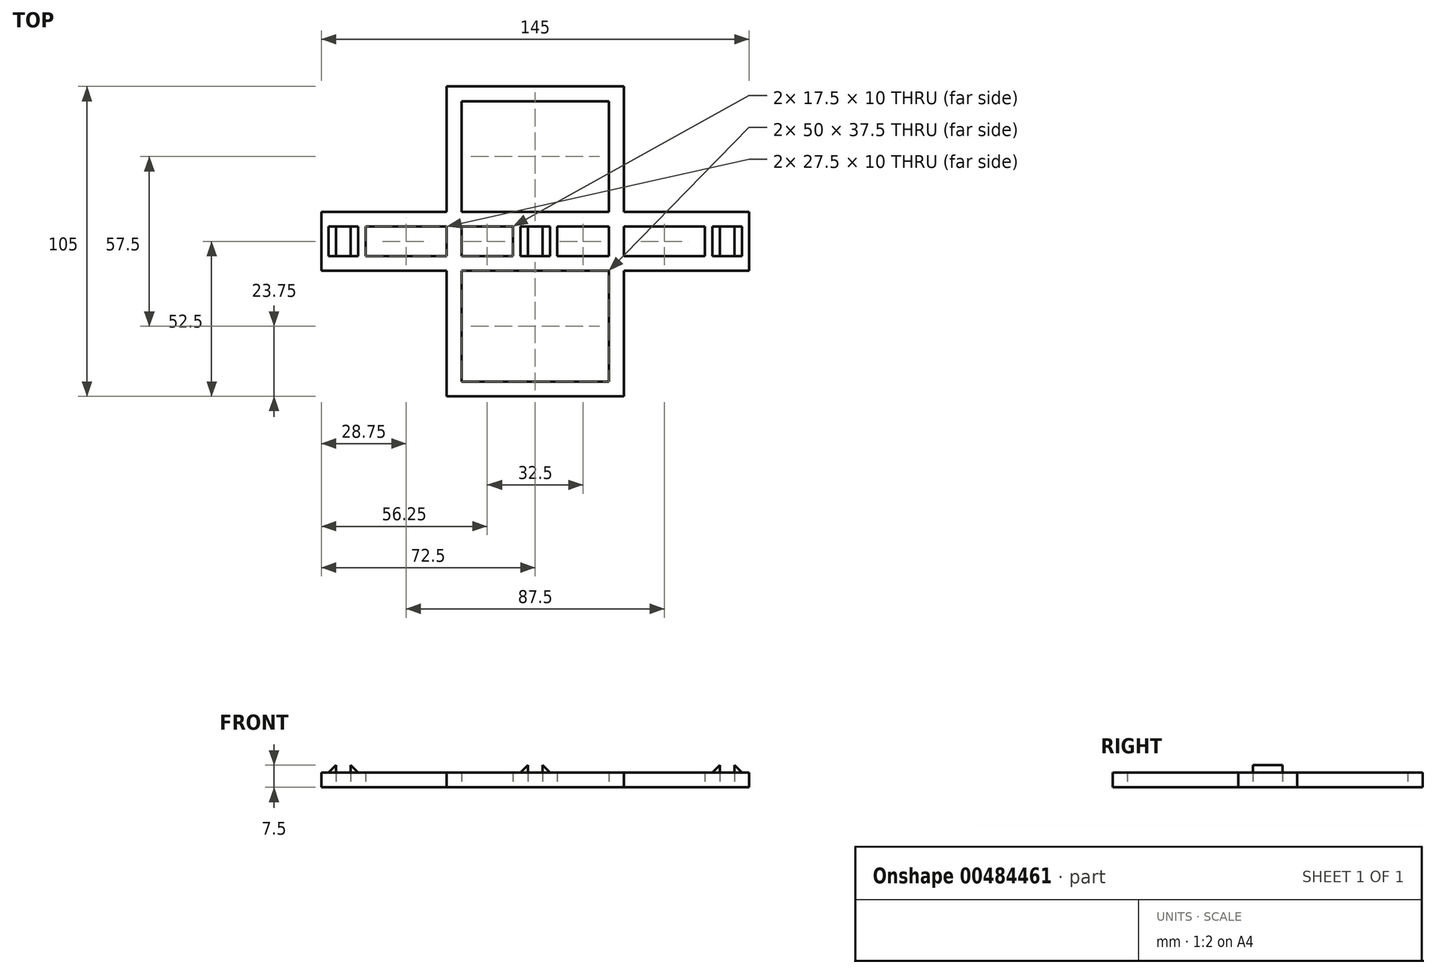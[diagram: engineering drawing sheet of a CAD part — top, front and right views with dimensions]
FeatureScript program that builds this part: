
annotation { "Feature Type Name" : "Feature", "Feature Type Description" : "" }
export const myFeature = defineFeature(function(context is Context, id is Id, definition is map)
    precondition{}
    {
        {
            var Q0;
            Q0=qCreatedBy(makeId("Top.planeOp"),FACE);
            var sketch = newSketch(context, id + "F0", { "sketchPlane" : qUnion([Q0])});
            skLineSegment(sketch, "E0.bottom", {"start": v(-2.5, 5) * mm, "end": v(2.5, 5) * mm});
            skLineSegment(sketch, "E0.top", {"start": v(-2.5, -5) * mm, "end": v(2.5, -5) * mm});
            skLineSegment(sketch, "E0.left", {"start": v(-2.5, 5) * mm, "end": v(-2.5, -5) * mm});
            skLineSegment(sketch, "E0.right", {"start": v(2.5, 5) * mm, "end": v(2.5, -5) * mm});
            skLineSegment(sketch, "E1.bottom", {"start": v(62.5, 5) * mm, "end": v(67.5, 5) * mm});
            skLineSegment(sketch, "E1.top", {"start": v(62.5, -5) * mm, "end": v(67.5, -5) * mm});
            skLineSegment(sketch, "E1.left", {"start": v(62.5, 5) * mm, "end": v(62.5, -5) * mm});
            skLineSegment(sketch, "E1.right", {"start": v(67.5, 5) * mm, "end": v(67.5, -5) * mm});
            skLineSegment(sketch, "E2.bottom", {"start": v(-67.5, 5) * mm, "end": v(-62.5, 5) * mm});
            skLineSegment(sketch, "E2.top", {"start": v(-67.5, -5) * mm, "end": v(-62.5, -5) * mm});
            skLineSegment(sketch, "E2.left", {"start": v(-67.5, 5) * mm, "end": v(-67.5, -5) * mm});
            skLineSegment(sketch, "E2.right", {"start": v(-62.5, 5) * mm, "end": v(-62.5, -5) * mm});
            skLineSegment(sketch, "E3.bottom", {"start": v(-72.5, 10) * mm, "end": v(72.5, 10) * mm});
            skLineSegment(sketch, "E3.top", {"start": v(-72.5, -10) * mm, "end": v(72.5, -10) * mm});
            skLineSegment(sketch, "E3.left", {"start": v(-72.5, 10) * mm, "end": v(-72.5, -10) * mm});
            skLineSegment(sketch, "E4.bottom", {"start": v(-57.5, 5) * mm, "end": v(-5, 5) * mm});
            skLineSegment(sketch, "E4.top", {"start": v(-57.5, -5) * mm, "end": v(-5, -5) * mm});
            skLineSegment(sketch, "E4.left", {"start": v(-57.5, 5) * mm, "end": v(-57.5, -5) * mm});
            skLineSegment(sketch, "E4.right", {"start": v(-5, 5) * mm, "end": v(-5, -5) * mm});
            skLineSegment(sketch, "E5.bottom", {"start": v(5, 5) * mm, "end": v(57.5, 5) * mm});
            skLineSegment(sketch, "E5.top", {"start": v(5, -5) * mm, "end": v(57.5, -5) * mm});
            skLineSegment(sketch, "E5.left", {"start": v(5, 5) * mm, "end": v(5, -5) * mm});
            skLineSegment(sketch, "E5.right", {"start": v(57.5, 5) * mm, "end": v(57.5, -5) * mm});
            skLineSegment(sketch, "E6.bottom", {"start": v(-25, 47.5) * mm, "end": v(25, 47.5) * mm});
            skLineSegment(sketch, "E6.top", {"start": v(-25, -47.5) * mm, "end": v(25, -47.5) * mm});
            skLineSegment(sketch, "E6.left", {"start": v(-25, 47.5) * mm, "end": v(-25, -47.5) * mm});
            skLineSegment(sketch, "E6.right", {"start": v(25, 47.5) * mm, "end": v(25, -47.5) * mm});
            skLineSegment(sketch, "E7.bottom", {"start": v(-30, 52.5) * mm, "end": v(30, 52.5) * mm});
            skLineSegment(sketch, "E7.top", {"start": v(-30, -52.5) * mm, "end": v(30, -52.5) * mm});
            skLineSegment(sketch, "E7.left", {"start": v(-30, 52.5) * mm, "end": v(-30, -52.5) * mm});
            skLineSegment(sketch, "E7.right", {"start": v(30, 52.5) * mm, "end": v(30, -52.5) * mm});
            skLineSegment(sketch, "E8", {"start": v(-57.5, 5) * mm, "end": v(-72.5, 5) * mm});
            skLineSegment(sketch, "E9", {"start": v(-57.5, -5) * mm, "end": v(-72.5, -5) * mm});
            skLineSegment(sketch, "E10", {"start": v(-5, 5) * mm, "end": v(5, 5) * mm});
            skLineSegment(sketch, "E11", {"start": v(-5, -5) * mm, "end": v(5, -5) * mm});
            skLineSegment(sketch, "E12", {"start": v(57.5, 5) * mm, "end": v(72.5, 5) * mm});
            skLineSegment(sketch, "E13", {"start": v(57.5, -5) * mm, "end": v(72.5, -5) * mm});
            skLineSegment(sketch, "E14", {"start": v(-7.5, 5) * mm, "end": v(-7.5, -5) * mm});
            skLineSegment(sketch, "E15", {"start": v(7.5, 5) * mm, "end": v(7.5, -5) * mm});
            skLineSegment(sketch, "E16.left", {"start": v(72.5, 10) * mm, "end": v(72.5, -10) * mm});
            skLineSegment(sketch, "E17", {"start": v(-70, 5) * mm, "end": v(-70, -5) * mm});
            skLineSegment(sketch, "E18", {"start": v(-60, 5) * mm, "end": v(-60, -5) * mm});
            skLineSegment(sketch, "E19", {"start": v(60, 5) * mm, "end": v(60, -5) * mm});
            skLineSegment(sketch, "E20", {"start": v(70, 5) * mm, "end": v(70, -5) * mm});
            skSolve(sketch);
        }
        {
            var Q0;
            Q0=makeQuery(id+"F0.imprint","IMPRINT",FACE,{"disambiguationData":[TD([[makeQuery(id+"F0.imprint","IMPRINT",EDGE,{"derivedFrom":sQuery(id+"F0.wireOp",EDGE,"E0.bottom")}),1.0]])]});
            var Q1;
            Q1=makeQuery(id+"F0.imprint","IMPRINT",FACE,{"disambiguationData":[TD([[makeQuery(id+"F0.imprint","IMPRINT",EDGE,{"derivedFrom":sQuery(id+"F0.wireOp",EDGE,"E2.bottom")}),1.0]])]});
            var Q2;
            {var subQ1=sQuery(id+"F0.wireOp",EDGE,"E6.bottom");Q2=makeQuery(id+"F0.imprint","IMPRINT",FACE,{"disambiguationData":[TD([[makeQuery(id+"F0.imprint","IMPRINT",EDGE,{"derivedFrom":subQ1}),1.0]])]});}
            var Q3;
            {var subQ0=sQuery(id+"F0.wireOp",EDGE,"E7.left");var subQ1=sQuery(id+"F0.wireOp",EDGE,"E3.bottom");var subQ2=makeQuery(id+"F0.imprint","INTERSECT",VERTEX,{"derivedFrom":[subQ1,subQ0]});Q3=makeQuery(id+"F0.imprint","IMPRINT",FACE,{"disambiguationData":[TD([[makeQuery(id+"F0.imprint","IMPRINT",EDGE,{"disambiguationData":[TD([[subQ2,-1.0]])],"derivedFrom":subQ1}),-1.0]])]});}
            var Q4;
            {var subQ0=sQuery(id+"F0.wireOp",EDGE,"E7.left");var subQ1=sQuery(id+"F0.wireOp",EDGE,"E3.top");var subQ2=makeQuery(id+"F0.imprint","INTERSECT",VERTEX,{"derivedFrom":[subQ1,subQ0]});Q4=makeQuery(id+"F0.imprint","IMPRINT",FACE,{"disambiguationData":[TD([[makeQuery(id+"F0.imprint","IMPRINT",EDGE,{"disambiguationData":[TD([[subQ2,-1.0]])],"derivedFrom":subQ1}),1.0]])]});}
            var Q5;
            {var subQ1=sQuery(id+"F0.wireOp",EDGE,"E6.top");Q5=makeQuery(id+"F0.imprint","IMPRINT",FACE,{"disambiguationData":[TD([[makeQuery(id+"F0.imprint","IMPRINT",EDGE,{"derivedFrom":subQ1}),-1.0]])]});}
            var Q6;
            {var subQ0=sQuery(id+"F0.wireOp",EDGE,"E7.right");var subQ1=sQuery(id+"F0.wireOp",EDGE,"E3.bottom");var subQ2=makeQuery(id+"F0.imprint","INTERSECT",VERTEX,{"derivedFrom":[subQ1,subQ0]});Q6=makeQuery(id+"F0.imprint","IMPRINT",FACE,{"disambiguationData":[TD([[makeQuery(id+"F0.imprint","IMPRINT",EDGE,{"disambiguationData":[TD([[subQ2,1.0]])],"derivedFrom":subQ1}),-1.0]])]});}
            var Q7;
            Q7=makeQuery(id+"F0.imprint","IMPRINT",FACE,{"disambiguationData":[TD([[makeQuery(id+"F0.imprint","IMPRINT",EDGE,{"derivedFrom":sQuery(id+"F0.wireOp",EDGE,"E1.bottom")}),1.0]])]});
            var Q8;
            {var subQ0=sQuery(id+"F0.wireOp",EDGE,"E7.right");var subQ1=sQuery(id+"F0.wireOp",EDGE,"E3.top");var subQ2=makeQuery(id+"F0.imprint","INTERSECT",VERTEX,{"derivedFrom":[subQ1,subQ0]});Q8=makeQuery(id+"F0.imprint","IMPRINT",FACE,{"disambiguationData":[TD([[makeQuery(id+"F0.imprint","IMPRINT",EDGE,{"disambiguationData":[TD([[subQ2,1.0]])],"derivedFrom":subQ1}),1.0]])]});}
            var Q9;
            {var subQ1=sQuery(id+"F0.wireOp",EDGE,"E3.bottom");var subQ7=sQuery(id+"F0.wireOp",EDGE,"E3.right");var subQ8=makeQuery(id+"F0.imprint","INTERSECT",VERTEX,{"derivedFrom":[subQ1,subQ7]});Q9=makeQuery(id+"F0.imprint","IMPRINT",FACE,{"disambiguationData":[TD([[makeQuery(id+"F0.imprint","IMPRINT",EDGE,{"disambiguationData":[TD([[subQ8,1.0]])],"derivedFrom":subQ1}),-1.0]])]});}
            var Q10;
            {var subQ0=sQuery(id+"F0.wireOp",EDGE,"E1.left");Q10=makeQuery(id+"F0.imprint","IMPRINT",FACE,{"disambiguationData":[TD([[makeQuery(id+"F0.imprint","IMPRINT",EDGE,{"derivedFrom":subQ0}),-1.0]])]});}
            var Q11;
            {var subQ0=sQuery(id+"F0.wireOp",EDGE,"E1.right");Q11=makeQuery(id+"F0.imprint","IMPRINT",FACE,{"disambiguationData":[TD([[makeQuery(id+"F0.imprint","IMPRINT",EDGE,{"derivedFrom":subQ0}),1.0]])]});}
            var Q12;
            {var subQ0=sQuery(id+"F0.wireOp",EDGE,"E3.right");var subQ1=sQuery(id+"F0.wireOp",EDGE,"E3.top");var subQ2=makeQuery(id+"F0.imprint","INTERSECT",VERTEX,{"derivedFrom":[subQ1,subQ0]});Q12=makeQuery(id+"F0.imprint","IMPRINT",FACE,{"disambiguationData":[TD([[makeQuery(id+"F0.imprint","IMPRINT",EDGE,{"disambiguationData":[TD([[subQ2,1.0]])],"derivedFrom":subQ1}),1.0]])]});}
            var Q13;
            {var subQ0=sQuery(id+"F0.wireOp",EDGE,"E6.left");var subQ1=sQuery(id+"F0.wireOp",EDGE,"E3.bottom");var subQ2=makeQuery(id+"F0.imprint","INTERSECT",VERTEX,{"derivedFrom":[subQ1,subQ0]});Q13=makeQuery(id+"F0.imprint","IMPRINT",FACE,{"disambiguationData":[TD([[makeQuery(id+"F0.imprint","IMPRINT",EDGE,{"disambiguationData":[TD([[subQ2,-1.0]])],"derivedFrom":subQ1}),-1.0]])]});}
            var Q14;
            {var subQ3=sQuery(id+"F0.wireOp",EDGE,"E6.left");var subQ6=sQuery(id+"F0.wireOp",EDGE,"E3.top");var subQ7=makeQuery(id+"F0.imprint","INTERSECT",VERTEX,{"derivedFrom":[subQ6,subQ3]});Q14=makeQuery(id+"F0.imprint","IMPRINT",FACE,{"disambiguationData":[TD([[makeQuery(id+"F0.imprint","IMPRINT",EDGE,{"disambiguationData":[TD([[subQ7,-1.0]])],"derivedFrom":subQ6}),1.0]])]});}
            var Q15;
            {var subQ0=sQuery(id+"F0.wireOp",EDGE,"E0.left");Q15=makeQuery(id+"F0.imprint","IMPRINT",FACE,{"disambiguationData":[TD([[makeQuery(id+"F0.imprint","IMPRINT",EDGE,{"derivedFrom":subQ0}),-1.0]])]});}
            var Q16;
            {var subQ0=sQuery(id+"F0.wireOp",EDGE,"E0.right");Q16=makeQuery(id+"F0.imprint","IMPRINT",FACE,{"disambiguationData":[TD([[makeQuery(id+"F0.imprint","IMPRINT",EDGE,{"derivedFrom":subQ0}),1.0]])]});}
            var Q17;
            {var subQ1=sQuery(id+"F0.wireOp",EDGE,"E3.bottom");var subQ7=sQuery(id+"F0.wireOp",EDGE,"E3.left");var subQ10=makeQuery(id+"F0.imprint","INTERSECT",VERTEX,{"derivedFrom":[subQ1,subQ7]});Q17=makeQuery(id+"F0.imprint","IMPRINT",FACE,{"disambiguationData":[TD([[makeQuery(id+"F0.imprint","IMPRINT",EDGE,{"disambiguationData":[TD([[subQ10,-1.0]])],"derivedFrom":subQ1}),-1.0]])]});}
            var Q18;
            {var subQ1=sQuery(id+"F0.wireOp",EDGE,"E3.top");var subQ5=sQuery(id+"F0.wireOp",EDGE,"E3.left");var subQ6=makeQuery(id+"F0.imprint","INTERSECT",VERTEX,{"derivedFrom":[subQ1,subQ5]});Q18=makeQuery(id+"F0.imprint","IMPRINT",FACE,{"disambiguationData":[TD([[makeQuery(id+"F0.imprint","IMPRINT",EDGE,{"disambiguationData":[TD([[subQ6,-1.0]])],"derivedFrom":subQ1}),1.0]])]});}
            var Q19;
            {var subQ0=sQuery(id+"F0.wireOp",EDGE,"E2.left");Q19=makeQuery(id+"F0.imprint","IMPRINT",FACE,{"disambiguationData":[TD([[makeQuery(id+"F0.imprint","IMPRINT",EDGE,{"derivedFrom":subQ0}),-1.0]])]});}
            var Q20;
            {var subQ0=sQuery(id+"F0.wireOp",EDGE,"E2.right");Q20=makeQuery(id+"F0.imprint","IMPRINT",FACE,{"disambiguationData":[TD([[makeQuery(id+"F0.imprint","IMPRINT",EDGE,{"derivedFrom":subQ0}),1.0]])]});}
            var Q21;
            {var subQ5=sQuery(id+"F0.wireOp",EDGE,"E17");Q21=makeQuery(id+"F0.imprint","IMPRINT",FACE,{"disambiguationData":[TD([[makeQuery(id+"F0.imprint","IMPRINT",EDGE,{"derivedFrom":subQ5}),-1.0]])]});}
            var Q22;
            {var subQ0=sQuery(id+"F0.wireOp",EDGE,"E4.left");Q22=makeQuery(id+"F0.imprint","IMPRINT",FACE,{"disambiguationData":[TD([[makeQuery(id+"F0.imprint","IMPRINT",EDGE,{"derivedFrom":subQ0}),-1.0]])]});}
            var Q23;
            {var subQ5=sQuery(id+"F0.wireOp",EDGE,"E3.bottom");var subQ10=sQuery(id+"F0.wireOp",EDGE,"E16.left");var subQ11=makeQuery(id+"F0.imprint","INTERSECT",VERTEX,{"derivedFrom":[subQ5,subQ10]});Q23=makeQuery(id+"F0.imprint","IMPRINT",FACE,{"disambiguationData":[TD([[makeQuery(id+"F0.imprint","IMPRINT",EDGE,{"disambiguationData":[TD([[subQ11,1.0]])],"derivedFrom":subQ5}),-1.0]])]});}
            var Q24;
            {var subQ5=sQuery(id+"F0.wireOp",EDGE,"E3.top");var subQ8=sQuery(id+"F0.wireOp",EDGE,"E16.left");var subQ9=makeQuery(id+"F0.imprint","INTERSECT",VERTEX,{"derivedFrom":[subQ5,subQ8]});Q24=makeQuery(id+"F0.imprint","IMPRINT",FACE,{"disambiguationData":[TD([[makeQuery(id+"F0.imprint","IMPRINT",EDGE,{"disambiguationData":[TD([[subQ9,1.0]])],"derivedFrom":subQ5}),1.0]])]});}
            var Q25;
            {var subQ0=sQuery(id+"F0.wireOp",EDGE,"E5.right");Q25=makeQuery(id+"F0.imprint","IMPRINT",FACE,{"disambiguationData":[TD([[makeQuery(id+"F0.imprint","IMPRINT",EDGE,{"derivedFrom":subQ0}),1.0]])]});}
            var Q26;
            {var subQ3=sQuery(id+"F0.wireOp",EDGE,"E20");Q26=makeQuery(id+"F0.imprint","IMPRINT",FACE,{"disambiguationData":[TD([[makeQuery(id+"F0.imprint","IMPRINT",EDGE,{"derivedFrom":subQ3}),1.0]])]});}
            var Q27;
            {var subQ0=sQuery(id+"F0.wireOp",EDGE,"E5.left");Q27=makeQuery(id+"F0.imprint","IMPRINT",FACE,{"disambiguationData":[TD([[makeQuery(id+"F0.imprint","IMPRINT",EDGE,{"derivedFrom":subQ0}),1.0]])]});}
            var Q28;
            {var subQ0=sQuery(id+"F0.wireOp",EDGE,"E4.right");Q28=makeQuery(id+"F0.imprint","IMPRINT",FACE,{"disambiguationData":[TD([[makeQuery(id+"F0.imprint","IMPRINT",EDGE,{"derivedFrom":subQ0}),-1.0]])]});}
            var Q29;
            {var subQ0=sQuery(id+"F0.wireOp",EDGE,"E7.left");var subQ1=sQuery(id+"F0.wireOp",EDGE,"E4.bottom");var subQ2=makeQuery(id+"F0.imprint","INTERSECT",VERTEX,{"derivedFrom":[subQ1,subQ0]});Q29=makeQuery(id+"F0.imprint","IMPRINT",FACE,{"disambiguationData":[TD([[makeQuery(id+"F0.imprint","IMPRINT",EDGE,{"disambiguationData":[TD([[subQ2,-1.0]])],"derivedFrom":subQ1}),-1.0]])]});}
            var Q30;
            {var subQ0=sQuery(id+"F0.wireOp",EDGE,"E6.right");var subQ1=sQuery(id+"F0.wireOp",EDGE,"E5.bottom");var subQ2=makeQuery(id+"F0.imprint","INTERSECT",VERTEX,{"derivedFrom":[subQ1,subQ0]});Q30=makeQuery(id+"F0.imprint","IMPRINT",FACE,{"disambiguationData":[TD([[makeQuery(id+"F0.imprint","IMPRINT",EDGE,{"disambiguationData":[TD([[subQ2,-1.0]])],"derivedFrom":subQ1}),-1.0]])]});}
            extrude(context, id + "F1", {"entities" : qUnion([Q0, Q1, Q2, Q3, Q4, Q5, Q6, Q7, Q8, Q9, Q10, Q11, Q12, Q13, Q14, Q15, Q16, Q17, Q18, Q19, Q20, Q21, Q22, Q23, Q24, Q25, Q26, Q27, Q28, Q29, Q30]), "depth" : 5 * mm});
        }
        {
            var Q0;
            {var subQ0=sQuery(id+"F0.wireOp",EDGE,"E2.left");Q0=makeQuery(id+"F0.imprint","IMPRINT",FACE,{"disambiguationData":[TD([[makeQuery(id+"F0.imprint","IMPRINT",EDGE,{"derivedFrom":subQ0}),-1.0]])]});}
            var Q1;
            {var subQ0=sQuery(id+"F0.wireOp",EDGE,"E2.right");Q1=makeQuery(id+"F0.imprint","IMPRINT",FACE,{"disambiguationData":[TD([[makeQuery(id+"F0.imprint","IMPRINT",EDGE,{"derivedFrom":subQ0}),1.0]])]});}
            var Q2;
            {var subQ0=sQuery(id+"F0.wireOp",EDGE,"E0.left");Q2=makeQuery(id+"F0.imprint","IMPRINT",FACE,{"disambiguationData":[TD([[makeQuery(id+"F0.imprint","IMPRINT",EDGE,{"derivedFrom":subQ0}),-1.0]])]});}
            var Q3;
            {var subQ0=sQuery(id+"F0.wireOp",EDGE,"E0.right");Q3=makeQuery(id+"F0.imprint","IMPRINT",FACE,{"disambiguationData":[TD([[makeQuery(id+"F0.imprint","IMPRINT",EDGE,{"derivedFrom":subQ0}),1.0]])]});}
            var Q4;
            {var subQ0=sQuery(id+"F0.wireOp",EDGE,"E1.left");Q4=makeQuery(id+"F0.imprint","IMPRINT",FACE,{"disambiguationData":[TD([[makeQuery(id+"F0.imprint","IMPRINT",EDGE,{"derivedFrom":subQ0}),-1.0]])]});}
            var Q5;
            {var subQ0=sQuery(id+"F0.wireOp",EDGE,"E1.right");Q5=makeQuery(id+"F0.imprint","IMPRINT",FACE,{"disambiguationData":[TD([[makeQuery(id+"F0.imprint","IMPRINT",EDGE,{"derivedFrom":subQ0}),1.0]])]});}
            extrude(context, id + "F2", {"entities" : qUnion([Q0, Q1, Q2, Q3, Q4, Q5]), "operationType" : NewBodyOperationType.ADD, "depth" : 7.5 * mm});
        }
        {
            var Q0;
            Q0=makeQuery(id+"F2.opExtrude","CAP_EDGE",EDGE,{"disambiguationData":[OSD([sQuery(id+"F0.wireOp",EDGE,"E20")])],"isStart":false});
            var Q1;
            Q1=makeQuery(id+"F2.opExtrude","CAP_EDGE",EDGE,{"disambiguationData":[OSD([sQuery(id+"F0.wireOp",EDGE,"E19")])],"isStart":false});
            var Q2;
            Q2=makeQuery(id+"F2.opExtrude","CAP_EDGE",EDGE,{"disambiguationData":[OSD([sQuery(id+"F0.wireOp",EDGE,"E5.left")])],"isStart":false});
            var Q3;
            Q3=makeQuery(id+"F2.opExtrude","CAP_EDGE",EDGE,{"disambiguationData":[OSD([sQuery(id+"F0.wireOp",EDGE,"E4.right")])],"isStart":false});
            var Q4;
            Q4=makeQuery(id+"F2.opExtrude","CAP_EDGE",EDGE,{"disambiguationData":[OSD([sQuery(id+"F0.wireOp",EDGE,"E18")])],"isStart":false});
            var Q5;
            Q5=makeQuery(id+"F2.opExtrude","CAP_EDGE",EDGE,{"disambiguationData":[OSD([sQuery(id+"F0.wireOp",EDGE,"E17")])],"isStart":false});
            chamfer(context, id + "F3", {"entities" : qUnion([Q0, Q1, Q2, Q3, Q4, Q5]), "width" : 2.5 * mm, "tangentPropagation" : true});
        }
    });
